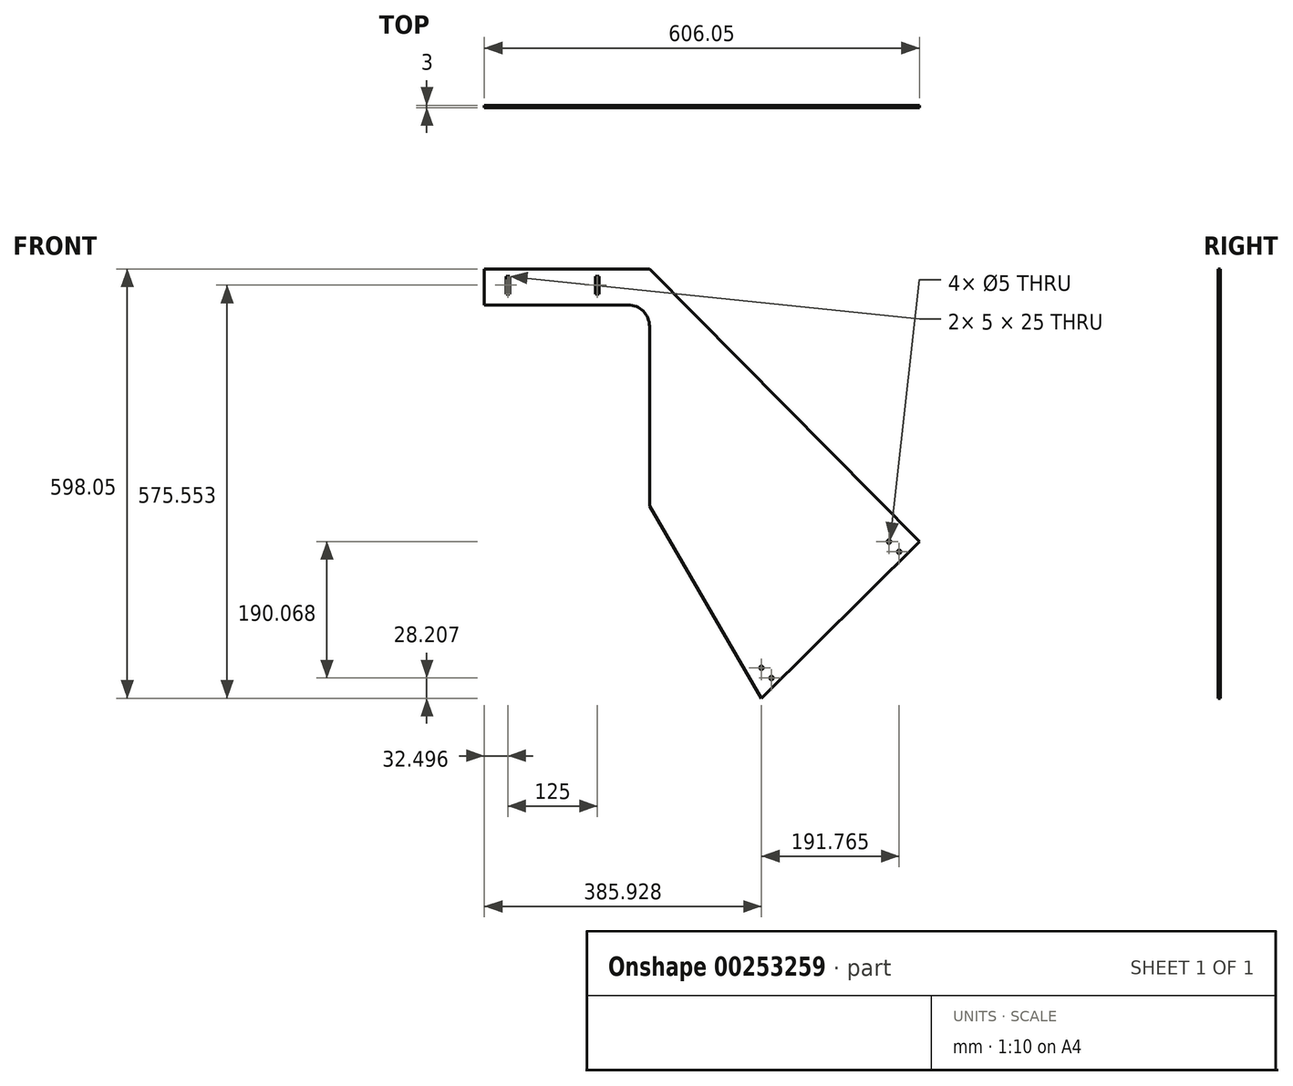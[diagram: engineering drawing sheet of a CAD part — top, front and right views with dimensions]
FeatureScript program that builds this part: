
annotation { "Feature Type Name" : "Feature", "Feature Type Description" : "" }
export const myFeature = defineFeature(function(context is Context, id is Id, definition is map)
    precondition{}
    {
        {
            var Q0;
            Q0=qCreatedBy(makeId("Front.planeOp"),FACE);
            var sketch = newSketch(context, id + "F0", { "sketchPlane" : qUnion([Q0])});
            skLineSegment(sketch, "E0", {"start": v(-334.93, 349.74) * mm, "end": v(-104.93, 349.74) * mm});
            skLineSegment(sketch, "E1", {"start": v(-104.93, 349.74) * mm, "end": v(271.12, -30.26) * mm});
            skLineSegment(sketch, "E2", {"start": v(271.12, -30.26) * mm, "end": v(50.78, -248.31) * mm});
            skLineSegment(sketch, "E3", {"start": v(-104.93, 19.74) * mm, "end": v(-104.93, 269.74) * mm});
            skLineSegment(sketch, "E4", {"start": v(-134.93, 299.74) * mm, "end": v(-334.93, 299.74) * mm});
            skLineSegment(sketch, "E5", {"start": v(-334.93, 299.74) * mm, "end": v(-334.93, 349.74) * mm});
            skLineSegment(sketch, "E6", {"start": v(-104.93, 19.74) * mm, "end": v(50.78, -248.31) * mm});
            skPoint(sketch, "E7.visualSharp", {"position": v(-104.93, 299.74) * mm});
            skArc(sketch, "E7.filletArc", {"start": v(-104.93, 269.74) * mm, "mid": v(-113.72, 290.96) * mm, "end": v(-134.93, 299.74) * mm});
            skSolve(sketch);
        }
        {
            var Q0;
            Q0=makeQuery(id+"F0.imprint","IMPRINT",FACE,{"disambiguationData":[TD([[makeQuery(id+"F0.imprint","IMPRINT",EDGE,{"derivedFrom":sQuery(id+"F0.wireOp",EDGE,"E0")}),-1.0]])]});
            extrude(context, id + "F1", {"entities" : qUnion([Q0]), "depth" : 3 * mm});
        }
        {
            var Q0;
            Q0=makeQuery(id+"F1.opExtrude","CAP_FACE",FACE,{"disambiguationData":[OSD([sQuery(id+"F0.wireOp",EDGE,"E0"),sQuery(id+"F0.wireOp",EDGE,"E1"),sQuery(id+"F0.wireOp",EDGE,"E2"),sQuery(id+"F0.wireOp",EDGE,"E3"),sQuery(id+"F0.wireOp",EDGE,"E4"),sQuery(id+"F0.wireOp",EDGE,"E5"),sQuery(id+"F0.wireOp",EDGE,"E6"),sQuery(id+"F0.wireOp",EDGE,"E7.filletArc")])],"isStart":false});
            var sketch = newSketch(context, id + "F2", { "sketchPlane" : qUnion([Q0])});
            skLineSegment(sketch, "E8.bottom", {"start": v(-304.93, 339.74) * mm, "end": v(-299.93, 339.74) * mm});
            skLineSegment(sketch, "E8.top", {"start": v(-304.93, 314.74) * mm, "end": v(-299.93, 314.74) * mm});
            skLineSegment(sketch, "E8.left", {"start": v(-304.93, 339.74) * mm, "end": v(-304.93, 314.74) * mm});
            skLineSegment(sketch, "E8.right", {"start": v(-299.93, 339.74) * mm, "end": v(-299.93, 314.74) * mm});
            skLineSegment(sketch, "E9.bottom", {"start": v(-179.93, 339.74) * mm, "end": v(-174.93, 339.74) * mm});
            skLineSegment(sketch, "E9.top", {"start": v(-179.93, 314.74) * mm, "end": v(-174.93, 314.74) * mm});
            skLineSegment(sketch, "E9.left", {"start": v(-179.93, 339.74) * mm, "end": v(-179.93, 314.74) * mm});
            skLineSegment(sketch, "E9.right", {"start": v(-174.93, 339.74) * mm, "end": v(-174.93, 314.74) * mm});
            skSolve(sketch);
        }
        {
            var Q0;
            Q0 = qSketchRegion(id + "F2", true);
            extrude(context, id + "F3", {"entities" : qUnion([Q0]), "operationType" : NewBodyOperationType.REMOVE, "endBound" : BoundingType.THROUGH_ALL, "oppositeDirection" : true, "depth" : 25 * mm});
        }
        {
            var Q0;
            Q0=makeQuery(id+"F1.opExtrude","CAP_FACE",FACE,{"disambiguationData":[OSD([sQuery(id+"F0.wireOp",EDGE,"E0"),sQuery(id+"F0.wireOp",EDGE,"E1"),sQuery(id+"F0.wireOp",EDGE,"E2"),sQuery(id+"F0.wireOp",EDGE,"E3"),sQuery(id+"F0.wireOp",EDGE,"E4"),sQuery(id+"F0.wireOp",EDGE,"E5"),sQuery(id+"F0.wireOp",EDGE,"E6"),sQuery(id+"F0.wireOp",EDGE,"E7.filletArc")])],"isStart":false});
            var sketch = newSketch(context, id + "F4", { "sketchPlane" : qUnion([Q0])});
            skCircle(sketch, "E10", {"center": v(228.7, -30.04) * mm, "radius": 2.5 * mm});
            skLineSegment(sketch, "E11", {"start": v(228.7, -30.04) * mm, "end": v(249.8, -51.36) * mm, "construction": true});
            skCircle(sketch, "E12", {"center": v(242.76, -44.25) * mm, "radius": 2.5 * mm});
            skLineSegment(sketch, "E13", {"start": v(160.95, -139.28) * mm, "end": v(112.01, -89.84) * mm, "construction": true});
            skCircle(sketch, "E14.MirrorC", {"center": v(51, -205.89) * mm, "radius": 2.5 * mm});
            skCircle(sketch, "E15.MirrorC", {"center": v(65.07, -220.1) * mm, "radius": 2.5 * mm});
            skSolve(sketch);
        }
        {
            var Q0;
            Q0 = qSketchRegion(id + "F4", true);
            extrude(context, id + "F5", {"entities" : qUnion([Q0]), "operationType" : NewBodyOperationType.REMOVE, "endBound" : BoundingType.THROUGH_ALL, "oppositeDirection" : true, "depth" : 25 * mm});
        }
    });
